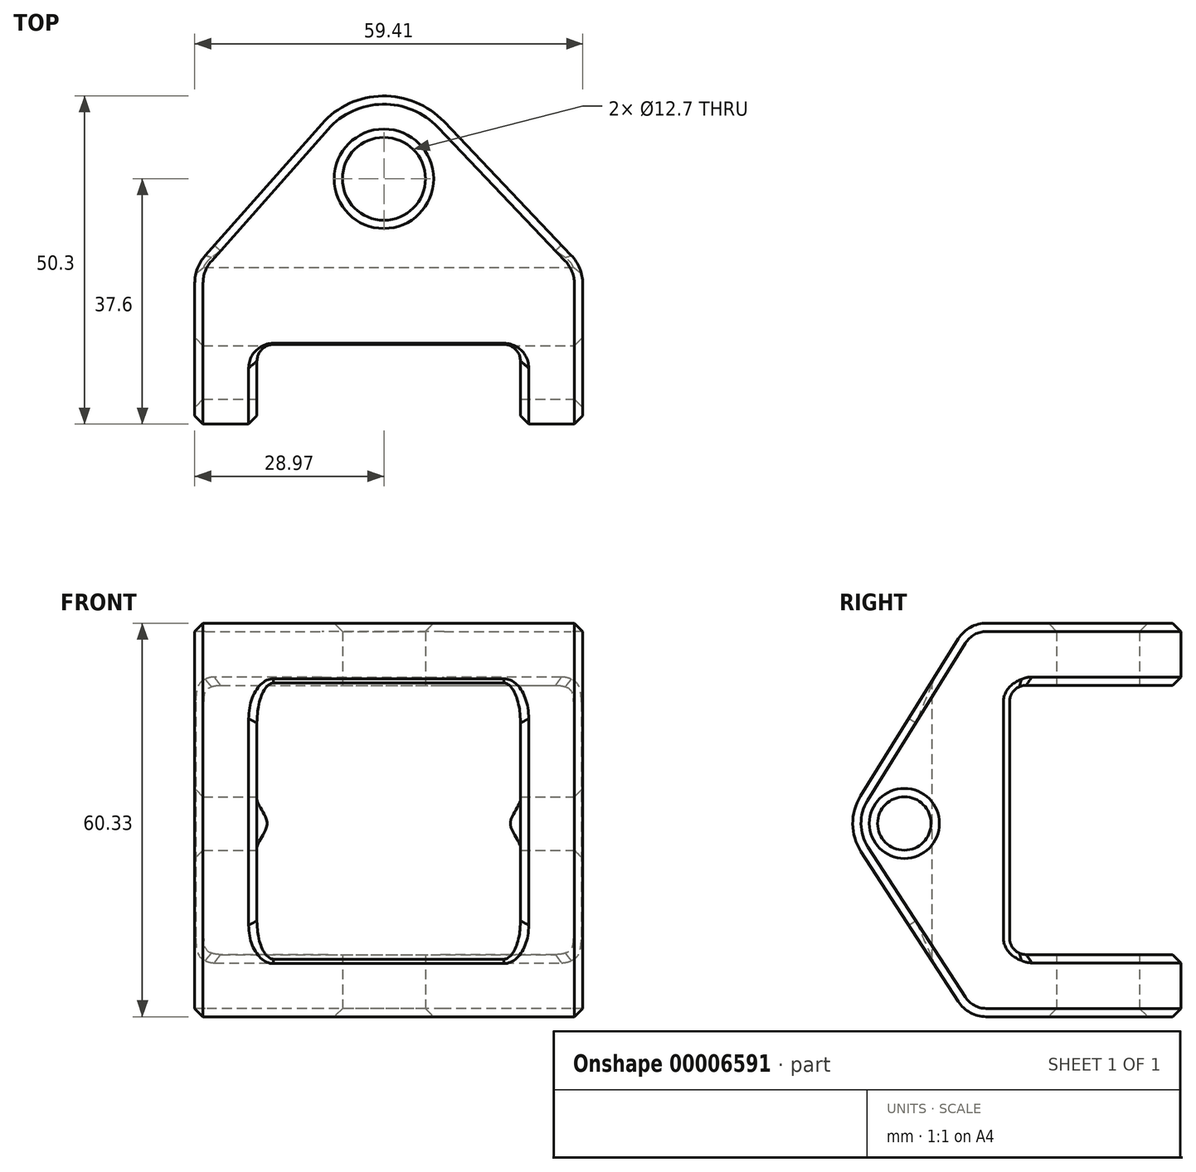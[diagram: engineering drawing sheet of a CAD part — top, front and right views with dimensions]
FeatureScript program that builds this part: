
annotation { "Feature Type Name" : "Feature", "Feature Type Description" : "" }
export const myFeature = defineFeature(function(context is Context, id is Id, definition is map)
    precondition{}
    {
        {
            var Q0;
            Q0=qCreatedBy(makeId("Top.planeOp"),FACE);
            var sketch = newSketch(context, id + "F0", { "sketchPlane" : qUnion([Q0])});
            skCircle(sketch, "E0", {"center": v(0, 0) * mm, "radius": 6.35 * mm});
            skLineSegment(sketch, "E1.top", {"start": v(-28.97, -19.92) * mm, "end": v(30.44, -19.92) * mm});
            skLineSegment(sketch, "E1.left", {"start": v(-28.97, -15.98) * mm, "end": v(-28.97, -19.92) * mm});
            skLineSegment(sketch, "E1.right", {"start": v(30.44, -16.11) * mm, "end": v(30.44, -19.92) * mm});
            skArc(sketch, "E2", {"start": v(9.2, 8.75) * mm, "mid": v(-0.23, 12.7) * mm, "end": v(-9.51, 8.42) * mm});
            skLineSegment(sketch, "E3", {"start": v(-27.37, -11.77) * mm, "end": v(-9.51, 8.42) * mm});
            skLineSegment(sketch, "E4", {"start": v(28.7, -11.73) * mm, "end": v(9.2, 8.75) * mm});
            skPoint(sketch, "E5.visualSharp", {"position": v(-28.97, -13.57) * mm});
            skArc(sketch, "E5.filletArc", {"start": v(-27.37, -11.77) * mm, "mid": v(-28.55, -13.73) * mm, "end": v(-28.97, -15.98) * mm});
            skPoint(sketch, "E6.visualSharp", {"position": v(30.44, -13.57) * mm});
            skArc(sketch, "E6.filletArc", {"start": v(30.44, -16.11) * mm, "mid": v(29.99, -13.75) * mm, "end": v(28.7, -11.73) * mm});
            skSolve(sketch);
        }
        {
            var Q0;
            Q0 = qSketchRegion(id + "F0", true);
            extrude(context, id + "F1", {"entities" : qUnion([Q0]), "depth" : 60.32 * mm});
        }
        {
            var Q0;
            Q0=makeQuery(id+"F1.opExtrude","SWEPT_FACE",FACE,{"disambiguationData":[OSD([sQuery(id+"F0.wireOp",EDGE,"E1.right")])]});
            var sketch = newSketch(context, id + "F2", { "sketchPlane" : qUnion([Q0])});
            skLineSegment(sketch, "E7.bottom", {"start": v(-11.03, 50.8) * mm, "end": v(33.75, 50.8) * mm});
            skLineSegment(sketch, "E7.top", {"start": v(-11.03, 9.53) * mm, "end": v(33.75, 9.53) * mm});
            skLineSegment(sketch, "E7.left", {"start": v(-13.57, 48.26) * mm, "end": v(-13.57, 12.07) * mm});
            skLineSegment(sketch, "E7.right", {"start": v(33.75, 50.8) * mm, "end": v(33.75, 9.53) * mm});
            skPoint(sketch, "E8.visualSharp", {"position": v(-13.57, 9.53) * mm});
            skArc(sketch, "E8.filletArc", {"start": v(-13.57, 12.07) * mm, "mid": v(-12.83, 10.27) * mm, "end": v(-11.03, 9.53) * mm});
            skPoint(sketch, "E9.visualSharp", {"position": v(-13.57, 50.8) * mm});
            skArc(sketch, "E9.filletArc", {"start": v(-11.03, 50.8) * mm, "mid": v(-12.83, 50.06) * mm, "end": v(-13.57, 48.26) * mm});
            skSolve(sketch);
        }
        {
            var Q0;
            Q0 = qSketchRegion(id + "F2", true);
            extrude(context, id + "F3", {"entities" : qUnion([Q0]), "operationType" : NewBodyOperationType.REMOVE, "endBound" : BoundingType.THROUGH_ALL, "oppositeDirection" : true, "depth" : 25.4 * mm});
        }
        {
            var Q0;
            Q0=makeQuery(id+"F1.opExtrude","SWEPT_FACE",FACE,{"disambiguationData":[OSD([sQuery(id+"F0.wireOp",EDGE,"E1.right")])]});
            var sketch = newSketch(context, id + "F4", { "sketchPlane" : qUnion([Q0])});
            skArc(sketch, "E10", {"start": v(-36.4, 33.8) * mm, "mid": v(-37.6, 29.55) * mm, "end": v(-36.33, 25.32) * mm});
            skLineSegment(sketch, "E11", {"start": v(-19.92, 0) * mm, "end": v(-36.33, 25.32) * mm});
            skLineSegment(sketch, "E12", {"start": v(-19.92, 60.33) * mm, "end": v(-36.4, 33.8) * mm});
            skCircle(sketch, "E13", {"center": v(-29.7, 29.62) * mm, "radius": 4.1 * mm});
            skLineSegment(sketch, "E14", {"start": v(-19.92, 60.33) * mm, "end": v(-19.92, 0) * mm});
            skSolve(sketch);
        }
        {
            var Q0;
            Q0 = qSketchRegion(id + "F4", true);
            var Q1;
            Q1=makeQuery(id+"F1.opExtrude","SWEPT_FACE",FACE,{"disambiguationData":[OSD([sQuery(id+"F0.wireOp",EDGE,"E1.left")])]});
            extrude(context, id + "F5", {"entities" : qUnion([Q0]), "operationType" : NewBodyOperationType.ADD, "endBound" : BoundingType.UP_TO_SURFACE, "oppositeDirection" : true, "endBoundEntityFace" : qUnion([Q1]), "depth" : 25.4 * mm});
        }
        {
            var Q0;
            Q0=makeQuery(id+"F5.boolean.opBoolean","MERGE",EDGE,{"derivedFrom":[makeQuery(id+"F1.opExtrude","CAP_EDGE",EDGE,{"disambiguationData":[OSD([sQuery(id+"F0.wireOp",EDGE,"E1.top")])],"isStart":true}),makeQuery(id+"F5.opExtrude","SWEPT_EDGE",EDGE,{"disambiguationData":[OSD([sQuery(id+"F0.wireOp",EDGE,"E1.right"),sQuery(id+"F4.wireOp",EDGE,"E11"),sQuery(id+"F4.wireOp",EDGE,"E14")])]})]});
            var Q1;
            Q1=makeQuery(id+"F5.boolean.opBoolean","MERGE",EDGE,{"derivedFrom":[makeQuery(id+"F1.opExtrude","CAP_EDGE",EDGE,{"disambiguationData":[OSD([sQuery(id+"F0.wireOp",EDGE,"E1.top")])],"isStart":false}),makeQuery(id+"F5.opExtrude","SWEPT_EDGE",EDGE,{"disambiguationData":[OSD([sQuery(id+"F0.wireOp",EDGE,"E1.right"),sQuery(id+"F4.wireOp",EDGE,"E12"),sQuery(id+"F4.wireOp",EDGE,"E14")])]})]});
            fillet(context, id + "F6", {"entities" : qUnion([Q0, Q1]), "radius" : 5.08 * mm, "tangentPropagation" : true, "allowEdgeOverflow" : false});
        }
        {
            var Q0;
            Q0=makeQuery(id+"F1.opExtrude","CAP_FACE",FACE,{"disambiguationData":[OSD([sQuery(id+"F0.wireOp",EDGE,"E0"),sQuery(id+"F0.wireOp",EDGE,"E1.top"),sQuery(id+"F0.wireOp",EDGE,"E1.left"),sQuery(id+"F0.wireOp",EDGE,"E1.right"),sQuery(id+"F0.wireOp",EDGE,"E2"),sQuery(id+"F0.wireOp",EDGE,"E3"),sQuery(id+"F0.wireOp",EDGE,"E4")])],"isStart":false});
            var sketch = newSketch(context, id + "F7", { "sketchPlane" : qUnion([Q0])});
            skLineSegment(sketch, "E15.bottom", {"start": v(-16.9, -25.4) * mm, "end": v(18.38, -25.4) * mm});
            skLineSegment(sketch, "E15.top", {"start": v(-19.44, -45.47) * mm, "end": v(20.92, -45.47) * mm});
            skLineSegment(sketch, "E15.left", {"start": v(-19.44, -27.94) * mm, "end": v(-19.44, -45.47) * mm});
            skLineSegment(sketch, "E15.right", {"start": v(20.92, -27.94) * mm, "end": v(20.92, -45.47) * mm});
            skPoint(sketch, "E16.visualSharp", {"position": v(-19.44, -25.4) * mm});
            skArc(sketch, "E16.filletArc", {"start": v(-16.9, -25.4) * mm, "mid": v(-18.7, -26.14) * mm, "end": v(-19.44, -27.94) * mm});
            skPoint(sketch, "E17.visualSharp", {"position": v(20.92, -25.4) * mm});
            skArc(sketch, "E17.filletArc", {"start": v(20.92, -27.94) * mm, "mid": v(20.17, -26.14) * mm, "end": v(18.38, -25.4) * mm});
            skSolve(sketch);
        }
        {
            var Q0;
            Q0 = qSketchRegion(id + "F7", true);
            extrude(context, id + "F8", {"entities" : qUnion([Q0]), "operationType" : NewBodyOperationType.REMOVE, "endBound" : BoundingType.THROUGH_ALL, "oppositeDirection" : true, "depth" : 25.4 * mm});
        }
        {
            var Q0;
            Q0=makeQuery(id+"F3.boolean.opBoolean","INTERSECT",EDGE,{"derivedFrom":[makeQuery(id+"F1.opExtrude","SWEPT_FACE",FACE,{"disambiguationData":[OSD([sQuery(id+"F0.wireOp",EDGE,"E3")])]}),makeQuery(id+"F3.opExtrude","SWEPT_FACE",FACE,{"disambiguationData":[OSD([sQuery(id+"F2.wireOp",EDGE,"E7.top")])]})]});
            var Q1;
            {var subQ0=sQuery(id+"F0.wireOp",EDGE,"E1.left");var subQ1=sQuery(id+"F0.wireOp",EDGE,"E3");Q1=makeQuery(id+"F3.boolean.opBoolean","SPLIT",EDGE,{"disambiguationData":[TD([makeQuery(id+"F1.opExtrude","SWEPT_FACE",FACE,{"disambiguationData":[OSD([subQ0])]}),makeQuery(id+"F1.opExtrude","SWEPT_FACE",FACE,{"disambiguationData":[OSD([subQ1])]}),makeQuery(id+"F3.opExtrude","SWEPT_FACE",FACE,{"disambiguationData":[OSD([sQuery(id+"F2.wireOp",EDGE,"E7.bottom")])]}),makeQuery(id+"F3.opExtrude","SWEPT_FACE",FACE,{"disambiguationData":[OSD([sQuery(id+"F2.wireOp",EDGE,"E7.top")])]}),makeQuery(id+"F3.opExtrude","SWEPT_FACE",FACE,{"disambiguationData":[OSD([sQuery(id+"F2.wireOp",EDGE,"E7.left")])]})])],"derivedFrom":makeQuery(id+"F1.opExtrude","SWEPT_EDGE",EDGE,{"disambiguationData":[OSD([subQ0,subQ1])]})});}
            var Q2;
            Q2=makeQuery(id+"F3.boolean.opBoolean","INTERSECT",EDGE,{"derivedFrom":[makeQuery(id+"F1.opExtrude","SWEPT_FACE",FACE,{"disambiguationData":[OSD([sQuery(id+"F0.wireOp",EDGE,"E3")])]}),makeQuery(id+"F3.opExtrude","SWEPT_FACE",FACE,{"disambiguationData":[OSD([sQuery(id+"F2.wireOp",EDGE,"E7.bottom")])]})]});
            var Q3;
            Q3=makeQuery(id+"F1.opExtrude","CAP_EDGE",EDGE,{"disambiguationData":[OSD([sQuery(id+"F0.wireOp",EDGE,"E3")])],"isStart":true});
            var Q4;
            Q4=makeQuery(id+"F1.opExtrude","CAP_EDGE",EDGE,{"disambiguationData":[OSD([sQuery(id+"F0.wireOp",EDGE,"E1.left")])],"isStart":true});
            var Q5;
            Q5=makeQuery(id+"F1.opExtrude","CAP_EDGE",EDGE,{"disambiguationData":[OSD([sQuery(id+"F0.wireOp",EDGE,"E3")])],"isStart":false});
            var Q6;
            Q6=makeQuery(id+"F1.opExtrude","CAP_EDGE",EDGE,{"disambiguationData":[OSD([sQuery(id+"F0.wireOp",EDGE,"E1.left")])],"isStart":false});
            var Q7;
            Q7=makeQuery(id+"F5.opExtrude","CAP_EDGE",EDGE,{"disambiguationData":[OSD([sQuery(id+"F4.wireOp",EDGE,"E12")])],"isStart":false});
            var Q8;
            Q8=makeQuery(id+"F8.boolean.opBoolean","INTERSECT",EDGE,{"derivedFrom":[makeQuery(id+"F5.opExtrude","SWEPT_FACE",FACE,{"disambiguationData":[OSD([sQuery(id+"F4.wireOp",EDGE,"E12")])]}),makeQuery(id+"F8.opExtrude","SWEPT_FACE",FACE,{"disambiguationData":[OSD([sQuery(id+"F7.wireOp",EDGE,"E15.right")])]})]});
            var Q9;
            Q9=makeQuery(id+"F8.boolean.opBoolean","INTERSECT",EDGE,{"derivedFrom":[makeQuery(id+"F5.opExtrude","SWEPT_FACE",FACE,{"disambiguationData":[OSD([sQuery(id+"F4.wireOp",EDGE,"E12")])]}),makeQuery(id+"F8.opExtrude","SWEPT_FACE",FACE,{"disambiguationData":[OSD([sQuery(id+"F7.wireOp",EDGE,"E15.left")])]})]});
            var Q10;
            Q10=makeQuery(id+"F8.boolean.opBoolean","MERGE",EDGE,{"derivedFrom":[makeQuery(id+"F5.boolean.opBoolean","MERGE",EDGE,{"derivedFrom":[makeQuery(id+"F1.opExtrude","CAP_EDGE",EDGE,{"disambiguationData":[OSD([sQuery(id+"F0.wireOp",EDGE,"E1.top")])],"isStart":false}),makeQuery(id+"F5.opExtrude","SWEPT_EDGE",EDGE,{"disambiguationData":[OSD([sQuery(id+"F0.wireOp",EDGE,"E1.right"),sQuery(id+"F4.wireOp",EDGE,"E12"),sQuery(id+"F4.wireOp",EDGE,"E14")])]})]}),makeQuery(id+"F8.opExtrude","CAP_EDGE",EDGE,{"disambiguationData":[OSD([sQuery(id+"F7.wireOp",EDGE,"E15.bottom")])],"isStart":true})]});
            var Q11;
            Q11=makeQuery(id+"F1.opExtrude","CAP_EDGE",EDGE,{"disambiguationData":[OSD([sQuery(id+"F0.wireOp",EDGE,"E1.right")])],"isStart":false});
            var Q12;
            Q12=makeQuery(id+"F5.opExtrude","CAP_EDGE",EDGE,{"disambiguationData":[OSD([sQuery(id+"F4.wireOp",EDGE,"E12")])],"isStart":true});
            var Q13;
            Q13=makeQuery(id+"F1.opExtrude","CAP_EDGE",EDGE,{"disambiguationData":[OSD([sQuery(id+"F0.wireOp",EDGE,"E1.right")])],"isStart":true});
            var Q14;
            Q14=makeQuery(id+"F3.boolean.opBoolean","MERGE",EDGE,{"derivedFrom":[makeQuery(id+"F1.opExtrude","SWEPT_EDGE",EDGE,{"disambiguationData":[OSD([sQuery(id+"F0.wireOp",EDGE,"E1.right"),sQuery(id+"F0.wireOp",EDGE,"E4")])]}),makeQuery(id+"F3.opExtrude","CAP_EDGE",EDGE,{"disambiguationData":[OSD([sQuery(id+"F2.wireOp",EDGE,"E7.left")])],"isStart":true})]});
            chamfer(context, id + "F9", {"entities" : qUnion([Q0, Q1, Q2, Q3, Q4, Q5, Q6, Q7, Q8, Q9, Q10, Q11, Q12, Q13, Q14]), "width" : 1.27 * mm, "tangentPropagation" : true});
        }
        {
            var Q0;
            Q0=makeQuery(id+"F1.opExtrude","CAP_EDGE",EDGE,{"disambiguationData":[OSD([sQuery(id+"F0.wireOp",EDGE,"E0")])],"isStart":true});
            var Q1;
            Q1=makeQuery(id+"F5.opExtrude","CAP_EDGE",EDGE,{"disambiguationData":[OSD([sQuery(id+"F4.wireOp",EDGE,"E13")])],"isStart":true});
            var Q2;
            Q2=makeQuery(id+"F1.opExtrude","CAP_EDGE",EDGE,{"disambiguationData":[OSD([sQuery(id+"F0.wireOp",EDGE,"E0")])],"isStart":false});
            var Q3;
            Q3=makeQuery(id+"F5.opExtrude","CAP_EDGE",EDGE,{"disambiguationData":[OSD([sQuery(id+"F4.wireOp",EDGE,"E13")])],"isStart":false});
            chamfer(context, id + "F10", {"entities" : qUnion([Q0, Q1, Q2, Q3]), "width" : 1.27 * mm, "tangentPropagation" : true});
        }
    });
